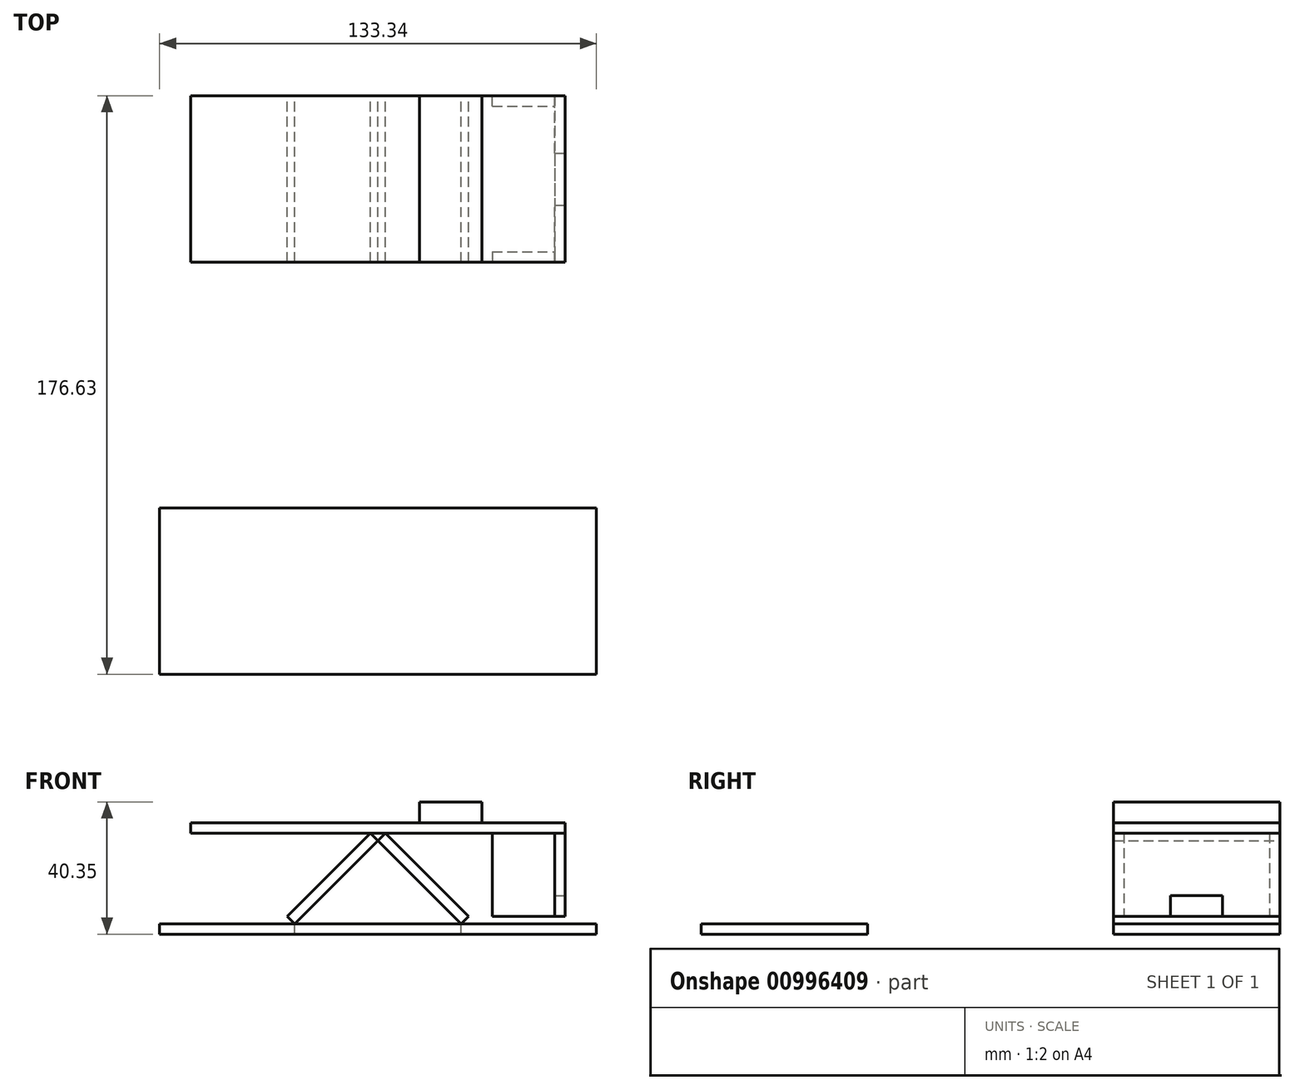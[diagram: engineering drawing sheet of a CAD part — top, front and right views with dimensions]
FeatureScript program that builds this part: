
annotation { "Feature Type Name" : "Feature", "Feature Type Description" : "" }
export const myFeature = defineFeature(function(context is Context, id is Id, definition is map)
    precondition{}
    {
        {
            var Q0;
            Q0=qCreatedBy(makeId("Front.planeOp"),FACE);
            var sketch = newSketch(context, id + "F0", { "sketchPlane" : qUnion([Q0])});
            skLineSegment(sketch, "E0.bottom", {"start": v(-25.4, 0) * mm, "end": v(25.4, 0) * mm});
            skLineSegment(sketch, "E0.top", {"start": v(-25.4, 3.17) * mm, "end": v(25.4, 3.17) * mm});
            skLineSegment(sketch, "E0.left", {"start": v(-25.4, 0) * mm, "end": v(-25.4, 3.17) * mm});
            skLineSegment(sketch, "E0.right", {"start": v(25.4, 0) * mm, "end": v(25.4, 3.17) * mm});
            skPoint(sketch, "E0.middle", {"position": v(0, 1.59) * mm});
            skLineSegment(sketch, "E1", {"start": v(-25.4, 3.17) * mm, "end": v(0, 28.57) * mm, "construction": true});
            skLineSegment(sketch, "E2", {"start": v(0, 28.58) * mm, "end": v(25.4, 3.17) * mm, "construction": true});
            skLineSegment(sketch, "E3.bottom", {"start": v(-27.65, 5.42) * mm, "end": v(-2.25, 30.82) * mm});
            skLineSegment(sketch, "E3.top", {"start": v(-25.4, 3.17) * mm, "end": v(0, 28.57) * mm});
            skLineSegment(sketch, "E3.left", {"start": v(-27.65, 5.42) * mm, "end": v(-25.4, 3.17) * mm});
            skLineSegment(sketch, "E3.right", {"start": v(-2.25, 30.82) * mm, "end": v(0, 28.57) * mm});
            skLineSegment(sketch, "E4.bottom", {"start": v(2.25, 30.82) * mm, "end": v(27.65, 5.42) * mm});
            skLineSegment(sketch, "E4.top", {"start": v(0, 28.57) * mm, "end": v(25.4, 3.17) * mm});
            skLineSegment(sketch, "E4.left", {"start": v(2.25, 30.82) * mm, "end": v(0, 28.57) * mm});
            skLineSegment(sketch, "E4.right", {"start": v(27.65, 5.42) * mm, "end": v(25.4, 3.18) * mm});
            skSolve(sketch);
        }
        {
            var Q0;
            Q0=makeQuery(id+"F0.imprint","IMPRINT",FACE,{"disambiguationData":[TD([[makeQuery(id+"F0.imprint","IMPRINT",EDGE,{"derivedFrom":sQuery(id+"F0.wireOp",EDGE,"E3.bottom")}),-1.0]])]});
            var Q1;
            Q1=makeQuery(id+"F0.imprint","IMPRINT",FACE,{"disambiguationData":[TD([[makeQuery(id+"F0.imprint","IMPRINT",EDGE,{"derivedFrom":sQuery(id+"F0.wireOp",EDGE,"E0.bottom")}),1.0]])]});
            var Q2;
            Q2=makeQuery(id+"F0.imprint","IMPRINT",FACE,{"disambiguationData":[TD([[makeQuery(id+"F0.imprint","IMPRINT",EDGE,{"derivedFrom":sQuery(id+"F0.wireOp",EDGE,"E4.bottom")}),-1.0]])]});
            extrude(context, id + "F1", {"entities" : qUnion([Q0, Q1, Q2]), "endBound" : BoundingType.SYMMETRIC, "depth" : 50.8 * mm, "offsetDistance" : 25.4 * mm});
        }
        {
            var Q0;
            Q0=makeQuery(id+"F1.opExtrude","SWEPT_EDGE",EDGE,{"disambiguationData":[OSD([sQuery(id+"F0.wireOp",EDGE,"E3.bottom"),sQuery(id+"F0.wireOp",EDGE,"E3.right")])]});
            var Q1;
            Q1=makeQuery(id+"F1.opExtrude","SWEPT_EDGE",EDGE,{"disambiguationData":[OSD([sQuery(id+"F0.wireOp",EDGE,"E4.bottom"),sQuery(id+"F0.wireOp",EDGE,"E4.left")])]});
            cPlane(context, id + "F2", {"entities" : qUnion([Q0, Q1]), "cplaneType" : CPlaneType.LINE_ANGLE, "offset" : 25.4 * mm, "angle" : 0 * degree, "width" : 152.4 * mm, "height" : 152.4 * mm});
        }
        {
            var Q0;
            Q0=qCreatedBy(id+"F2.planeOp",FACE);
            var sketch = newSketch(context, id + "F3", { "sketchPlane" : qUnion([Q0])});
            skLineSegment(sketch, "E5.bottom", {"start": v(-57.15, -25.4) * mm, "end": v(57.15, -25.4) * mm});
            skLineSegment(sketch, "E5.top", {"start": v(-57.15, 25.4) * mm, "end": v(57.15, 25.4) * mm});
            skLineSegment(sketch, "E5.left", {"start": v(-57.15, -25.4) * mm, "end": v(-57.15, 25.4) * mm});
            skLineSegment(sketch, "E5.right", {"start": v(57.15, -25.4) * mm, "end": v(57.15, 25.4) * mm});
            skPoint(sketch, "E5.middle", {"position": v(0, 0) * mm});
            skSolve(sketch);
        }
        {
            var Q0;
            Q0 = qSketchRegion(id + "F3", true);
            extrude(context, id + "F4", {"entities" : qUnion([Q0]), "oppositeDirection" : true, "depth" : 3.17 * mm, "offsetDistance" : 25.4 * mm});
        }
        {
            var Q0;
            Q0=makeQuery(id+"F4.opExtrude","SWEPT_FACE",FACE,{"disambiguationData":[OSD([sQuery(id+"F3.wireOp",EDGE,"E5.right")])]});
            var sketch = newSketch(context, id + "F5", { "sketchPlane" : qUnion([Q0])});
            skLineSegment(sketch, "E6.bottom", {"start": v(-25.4, 30.82) * mm, "end": v(25.4, 30.82) * mm});
            skLineSegment(sketch, "E6.top", {"start": v(-25.4, 5.42) * mm, "end": v(-7.94, 5.42) * mm});
            skLineSegment(sketch, "E6.left", {"start": v(-25.4, 30.82) * mm, "end": v(-25.4, 5.42) * mm});
            skLineSegment(sketch, "E6.right", {"start": v(25.4, 30.82) * mm, "end": v(25.4, 5.42) * mm});
            skLineSegment(sketch, "E7.top", {"start": v(7.94, 11.77) * mm, "end": v(-7.94, 11.77) * mm});
            skLineSegment(sketch, "E7.left", {"start": v(7.94, 5.42) * mm, "end": v(7.94, 11.77) * mm});
            skLineSegment(sketch, "E7.right", {"start": v(-7.94, 5.42) * mm, "end": v(-7.94, 11.77) * mm});
            skPoint(sketch, "E7.middle", {"position": v(0, 8.6) * mm});
            skPoint(sketch, "E7.middle.positionSnap0", {"position": v(0, 5.42) * mm});
            skPoint(sketch, "E7.centerSnap0", {"position": v(0, 5.42) * mm});
            skLineSegment(sketch, "E8.trimOffspring", {"start": v(7.94, 5.42) * mm, "end": v(25.4, 5.42) * mm});
            skSolve(sketch);
        }
        {
            var Q0;
            Q0 = qSketchRegion(id + "F5", true);
            extrude(context, id + "F6", {"entities" : qUnion([Q0]), "oppositeDirection" : true, "depth" : 3.17 * mm, "offsetDistance" : 25.4 * mm});
        }
        {
            var Q0;
            Q0=makeQuery(id+"F4.opExtrude","SWEPT_FACE",FACE,{"disambiguationData":[OSD([sQuery(id+"F3.wireOp",EDGE,"E5.top")])]});
            var sketch = newSketch(context, id + "F7", { "sketchPlane" : qUnion([Q0])});
            skLineSegment(sketch, "E9.bottom", {"start": v(53.98, 30.82) * mm, "end": v(34.93, 30.82) * mm});
            skLineSegment(sketch, "E9.top", {"start": v(53.98, 5.42) * mm, "end": v(34.93, 5.42) * mm});
            skLineSegment(sketch, "E9.left", {"start": v(53.98, 30.82) * mm, "end": v(53.98, 5.42) * mm});
            skLineSegment(sketch, "E9.right", {"start": v(34.93, 30.82) * mm, "end": v(34.93, 5.42) * mm});
            skSolve(sketch);
        }
        {
            var Q0;
            Q0 = qSketchRegion(id + "F7", true);
            extrude(context, id + "F8", {"entities" : qUnion([Q0]), "oppositeDirection" : true, "depth" : 3.17 * mm, "offsetDistance" : 25.4 * mm});
        }
        {
            var Q0;
            Q0=makeQuery(id+"F8.opExtrude","SWEPT_BODY",BODY,{"disambiguationData":[OSD([sQuery(id+"F7.wireOp",EDGE,"E9.bottom"),sQuery(id+"F7.wireOp",EDGE,"E9.top"),sQuery(id+"F7.wireOp",EDGE,"E9.left"),sQuery(id+"F7.wireOp",EDGE,"E9.right")])]});
            var Q1;
            Q1=qCreatedBy(makeId("Front.planeOp"),FACE);
            mirror(context, id + "F9", {"entities" : qUnion([Q0]), "mirrorPlane" : qUnion([Q1])});
        }
        {
            var Q0;
            Q0=makeQuery(id+"F4.opExtrude","CAP_FACE",FACE,{"disambiguationData":[OSD([sQuery(id+"F3.wireOp",EDGE,"E5.bottom"),sQuery(id+"F3.wireOp",EDGE,"E5.top"),sQuery(id+"F3.wireOp",EDGE,"E5.left"),sQuery(id+"F3.wireOp",EDGE,"E5.right")])],"isStart":false});
            var sketch = newSketch(context, id + "F10", { "sketchPlane" : qUnion([Q0])});
            skLineSegment(sketch, "E10.bottom", {"start": v(12.7, 25.4) * mm, "end": v(31.75, 25.4) * mm});
            skLineSegment(sketch, "E10.top", {"start": v(12.7, -25.4) * mm, "end": v(31.75, -25.4) * mm});
            skLineSegment(sketch, "E10.left", {"start": v(12.7, 25.4) * mm, "end": v(12.7, -25.4) * mm});
            skLineSegment(sketch, "E10.right", {"start": v(31.75, 25.4) * mm, "end": v(31.75, -25.4) * mm});
            skPoint(sketch, "E10.middle", {"position": v(22.23, 0) * mm});
            skSolve(sketch);
        }
        {
            var Q0;
            Q0 = qSketchRegion(id + "F10", true);
            extrude(context, id + "F11", {"entities" : qUnion([Q0]), "depth" : 6.35 * mm, "offsetDistance" : 25.4 * mm});
        }
        {
            var Q0;
            Q0=qCreatedBy(makeId("Top.planeOp"),FACE);
            var sketch = newSketch(context, id + "F12", { "sketchPlane" : qUnion([Q0])});
            skLineSegment(sketch, "E11.bottom", {"start": v(66.68, -100.43) * mm, "end": v(-66.67, -100.43) * mm});
            skLineSegment(sketch, "E11.top", {"start": v(66.68, -151.23) * mm, "end": v(-66.68, -151.23) * mm});
            skLineSegment(sketch, "E11.left", {"start": v(66.68, -100.43) * mm, "end": v(66.68, -151.23) * mm});
            skLineSegment(sketch, "E11.right", {"start": v(-66.68, -100.43) * mm, "end": v(-66.68, -151.23) * mm});
            skPoint(sketch, "E11.middle", {"position": v(0, -125.83) * mm});
            skSolve(sketch);
        }
        {
            var Q0;
            Q0 = qSketchRegion(id + "F12", true);
            extrude(context, id + "F13", {"entities" : qUnion([Q0]), "depth" : 3.17 * mm, "offsetDistance" : 25.4 * mm});
        }
    });
